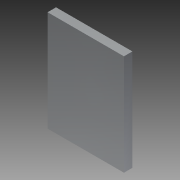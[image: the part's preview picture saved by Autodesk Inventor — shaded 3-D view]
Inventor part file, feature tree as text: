
AUTODESK INVENTOR PART (.ipt)
format: ipt  version: 2015 (Build 190159000, 159)  size: 72,704 bytes
history: native  units: mm
features: extrude x1, sketch x1
ambient origin geometry x8: Origin, YZ Plane, XZ Plane, XY Plane, X Axis, Y Axis, Z Axis, Center Point
bodies: Solid1 (feature_tree)
feature tree (2):
  extrude  "Extrusion1"  Depth=95.0mm
  sketch  "Sketch1"  dims[d0=72.0mm d1=95.0mm d2=8.0mm d3=0.0mm]
